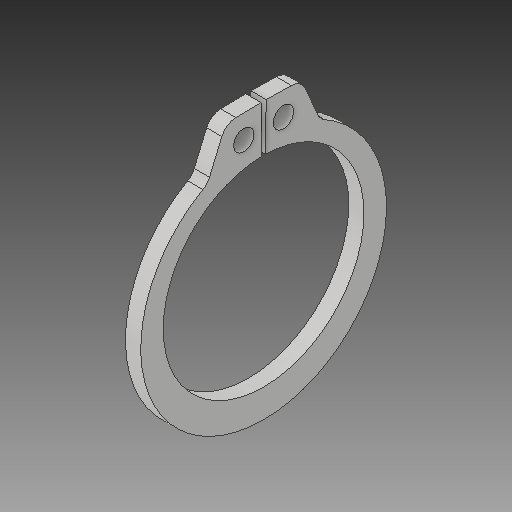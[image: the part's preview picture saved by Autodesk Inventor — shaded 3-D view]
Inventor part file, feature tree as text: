
AUTODESK INVENTOR PART (.ipt)
format: ipt  version: 2019 (Build 230136000, 136)  size: 114,688 bytes
history: native  units: in
note: dims shown in document units (in); Inventor stores cm internally (conversion verified against a paired STEP export)
features: fillet x1
ambient origin geometry x8: Origin, YZ Plane, XZ Plane, XY Plane, X Axis, Y Axis, Z Axis, Center Point
bodies: Solid1 (feature_tree)
feature tree (1):
  fillet  "Fillet1"  [1 undecoded]
note: 1 required parameter value undecoded (feature->parameter linkage not recoverable at this tier; creation-order binding heuristic only, values carry confidence <= 0.55)
